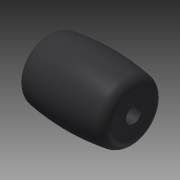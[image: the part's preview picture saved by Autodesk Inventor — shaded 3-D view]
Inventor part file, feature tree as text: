
AUTODESK INVENTOR PART (.ipt)
format: ipt  version: 2015 (Build 190159000, 159)  size: 145,920 bytes
history: native  units: in
note: dims shown in document units (in); Inventor stores cm internally (conversion verified against a paired STEP export)
features: revolve x1, other x1, imported_body x1
ambient origin geometry x8: Origin, YZ Plane, XZ Plane, XY Plane, X Axis, Y Axis, Z Axis, Center Point
bodies: Body1 (feature_tree)
feature tree (3):
  revolve  "Revolve1"  [1 undecoded]
  other  "tetrix_731132_roller1"
  imported_body  "Base1"
note: 1 required parameter value undecoded (feature->parameter linkage not recoverable at this tier; creation-order binding heuristic only, values carry confidence <= 0.55)
